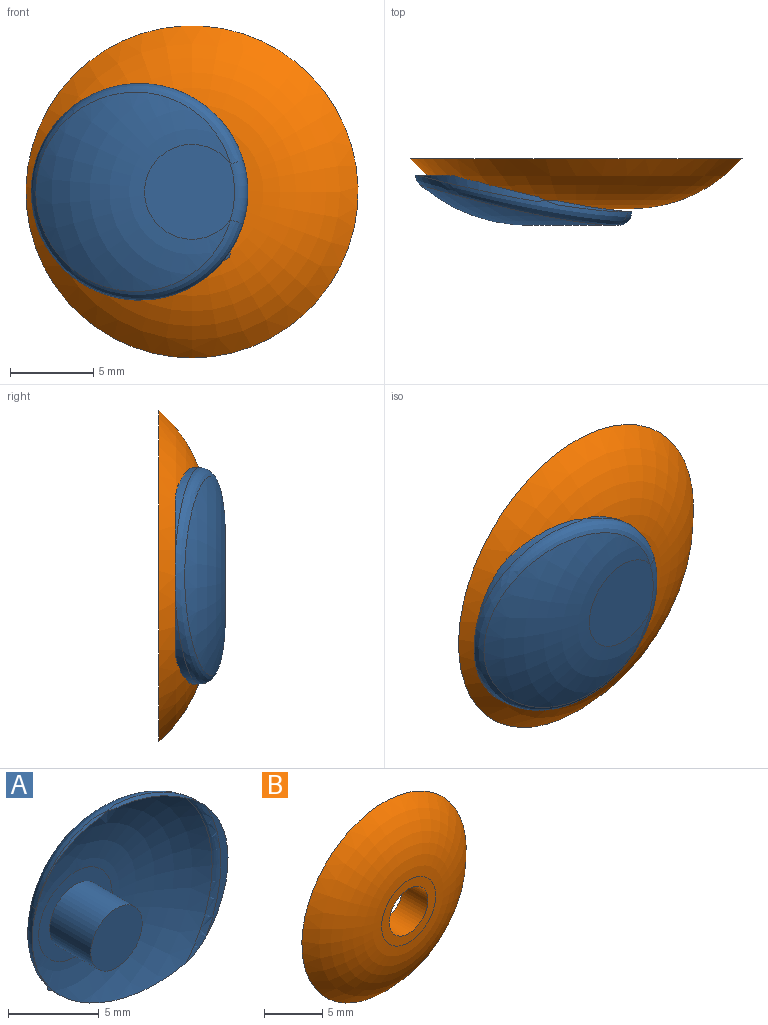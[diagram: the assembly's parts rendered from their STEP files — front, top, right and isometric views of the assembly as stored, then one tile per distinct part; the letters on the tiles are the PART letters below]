
ASSEMBLY  parts=2 mates=1
PART A: 15 faces, bbox 18.6x4.1x18.9 mm
  f0: plane 5.72x5.43mm, normal (0,1,0), area 25mm2, adj f1,f14
  f1: torus R=5.72mm, axis (0,-1,0), area 4.7mm2, adj f0,f2,f13
  f2: cylinder r=6.52mm len=4.4mm, axis (0,1,0), area 0.1mm2, adj f1,f3,f13
  f3: torus R=2.86mm, axis (0,1,0), area 109.4mm2, adj f2,f4,f5,f7,f8,f9,f10
  f4: cylinder r=6.52mm len=5.7mm, axis (0,1,0), area 1mm2, adj f3,f13
  f5: cylinder r=6.52mm len=6.8mm, axis (0,1,0), area 2.5mm2, adj f3,f6,f7,f13
  f6: plane 8.81x1.76mm, normal (0,-1,0), area 3.5mm2, adj f5,f7,f8,f13
  f7: torus R=9.12mm, axis (0,-1,0), area 5.7mm2, adj f3,f5,f6,f8
  f8: cylinder r=6.52mm len=7.7mm, axis (0,1,0), area 2.8mm2, adj f3,f6,f7,f13
  f9: cylinder r=6.52mm len=4.8mm, axis (0,1,0), area 0.9mm2, adj f3,f13
  f10: plane 5.72x5.72mm, normal (0,-1,0), area 13.1mm2, adj f3,f11
  f11: cylinder r=2mm len=4mm, axis (0,1,0), area 40.2mm2, adj f10,f12
  f12: plane 4x4mm, normal (0,-1,0), area 12.6mm2, adj f11
  f13: bspline ~13.04x12.75mm, area 34.4mm2, adj f1,f2,f4,f5,f6,f8,f9,f14
  f14: torus R=2.86mm, axis (0,1,0), area 94.2mm2, adj f0,f13
PART B: 4 faces, bbox 20x3x20 mm
  f0: cylinder r=2.35mm len=4.7mm, axis (0,1,0), area 44.3mm2, adj f1,f2
  f1: plane 6.58x6.58mm, normal (0,-1,0), area 16.7mm2, adj f0,f3
  f2: plane 20x20mm, normal (0,1,0), area 296.8mm2, adj f0,f3
  f3: torus R=3.29mm, axis (0,1,0), area 326.2mm2, adj f1,f2
PLACE A rot(axis=(0,0,1),180deg) t=(-28.39,-5.88,4.94)mm
PLACE B t=(-28.39,-1.88,4.94)mm
MATE revolute A.f11 <-> B.f0  axis (0,-1,0) through (-28.39,-1.88,4.94)mm
